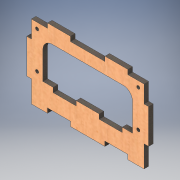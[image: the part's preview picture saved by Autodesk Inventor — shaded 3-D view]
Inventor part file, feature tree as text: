
AUTODESK INVENTOR PART (.ipt)
format: ipt  version: 2019 (Build 230136000, 136)  size: 188,416 bytes
history: native  units: mm
features: other x1, extrude x1, fillet x1, hole x1, sketch x1
ambient origin geometry x8: Origin, YZ Plane, XZ Plane, XY Plane, X Axis, Y Axis, Z Axis, Center Point
bodies: Body1 (feature_tree)
feature tree (5):
  other  "Твердое тело1"
  extrude  "Выдавливание1"  Depth=30.0mm
  fillet  "Сопряжение1"  Radius=10.0mm
  hole  "Отверстие1"  [1 undecoded]
  sketch  "Эскиз2"
note: 1 required parameter value undecoded (feature->parameter linkage not recoverable at this tier; creation-order binding heuristic only, values carry confidence <= 0.55)
